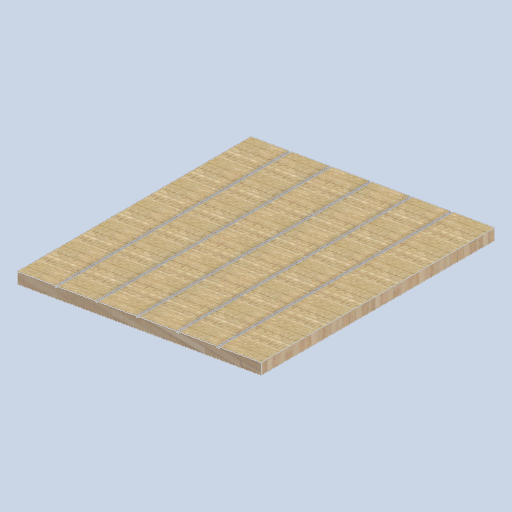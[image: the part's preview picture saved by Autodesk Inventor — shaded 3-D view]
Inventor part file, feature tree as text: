
AUTODESK INVENTOR PART (.ipt)
format: ipt  version: 2024.2 (Build 282272000, 272)  size: 253,440 bytes
history: native  units: in
note: dims shown in document units (in); Inventor stores cm internally (conversion verified against a paired STEP export)
features: sketch x4, other x3, plane x3
ambient origin geometry x8: Origin, YZ Plane, XZ Plane, XY Plane, X Axis, Y Axis, Z Axis, Center Point
bodies: Solid1 (feature_tree)
feature tree (10):
  other  "eave_panel_side__MIR.ipt"
  other  "Solid1::eave_panel_side__MIR.ipt"
  other  "TaggingFeature1"
  sketch  "Sketch1"  dims[d0=0.3937in]
  sketch  "Sketch2"
  sketch  "Sketch3"
  sketch  "Sketch4"
  plane  "Work Plane1"
  plane  "Work Plane2"
  plane  "Work Plane3"
